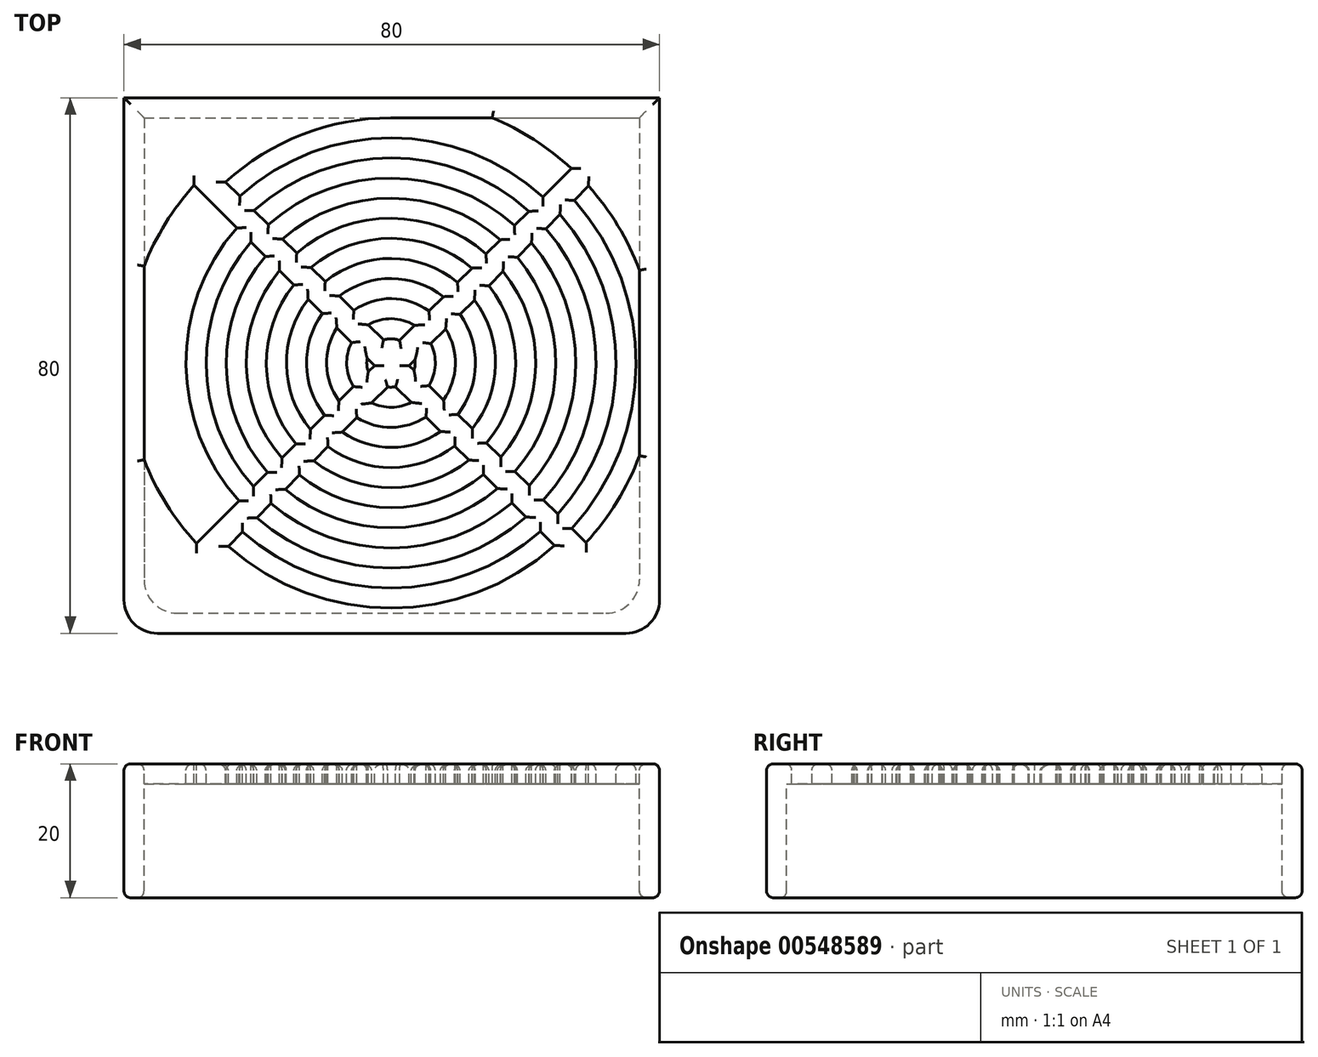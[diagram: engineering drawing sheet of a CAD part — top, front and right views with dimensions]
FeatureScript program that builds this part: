
annotation { "Feature Type Name" : "Feature", "Feature Type Description" : "" }
export const myFeature = defineFeature(function(context is Context, id is Id, definition is map)
    precondition{}
    {
        {
            var Q0;
            Q0=qCreatedBy(makeId("Front.planeOp"),FACE);
            var sketch = newSketch(context, id + "F0", { "sketchPlane" : qUnion([Q0])});
            skLineSegment(sketch, "E0.bottom", {"start": v(0, 0) * mm, "end": v(80, 0) * mm});
            skLineSegment(sketch, "E0.top", {"start": v(0, 20) * mm, "end": v(80, 20) * mm});
            skLineSegment(sketch, "E0.left", {"start": v(0, 0) * mm, "end": v(0, 20) * mm});
            skLineSegment(sketch, "E0.right", {"start": v(80, 0) * mm, "end": v(80, 20) * mm});
            skSolve(sketch);
        }
        {
            var Q0;
            Q0 = qSketchRegion(id + "F0", true);
            extrude(context, id + "F1", {"entities" : qUnion([Q0]), "depth" : 3 * mm, "offsetDistance" : 25 * mm});
        }
        {
            var Q0;
            Q0=makeQuery(id+"F1.opExtrude","SWEPT_FACE",FACE,{"disambiguationData":[OSD([sQuery(id+"F0.wireOp",EDGE,"E0.top")])]});
            var sketch = newSketch(context, id + "F2", { "sketchPlane" : qUnion([Q0])});
            skLineSegment(sketch, "E1.bottom", {"start": v(0, 0) * mm, "end": v(80, 0) * mm});
            skLineSegment(sketch, "E1.top", {"start": v(0, -80) * mm, "end": v(80, -80) * mm});
            skLineSegment(sketch, "E1.left", {"start": v(0, 0) * mm, "end": v(0, -80) * mm});
            skLineSegment(sketch, "E1.right", {"start": v(80, 0) * mm, "end": v(80, -80) * mm});
            skLineSegment(sketch, "E2.bottom", {"start": v(3, -3) * mm, "end": v(77, -3) * mm});
            skLineSegment(sketch, "E2.top", {"start": v(3, -77) * mm, "end": v(77, -77) * mm});
            skLineSegment(sketch, "E2.left", {"start": v(3, -3) * mm, "end": v(3, -77) * mm});
            skLineSegment(sketch, "E2.right", {"start": v(77, -3) * mm, "end": v(77, -77) * mm});
            skSolve(sketch);
        }
        {
            var Q0;
            Q0 = qSketchRegion(id + "F2", true);
            extrude(context, id + "F3", {"entities" : qUnion([Q0]), "operationType" : NewBodyOperationType.ADD, "oppositeDirection" : true, "depth" : 20 * mm, "offsetDistance" : 25 * mm});
        }
        {
            var Q0;
            Q0=makeQuery(id+"F3.opExtrude","SWEPT_EDGE",EDGE,{"disambiguationData":[OSD([sQuery(id+"F2.wireOp",EDGE,"E1.top"),sQuery(id+"F2.wireOp",EDGE,"E1.left")])]});
            var Q1;
            Q1=makeQuery(id+"F3.opExtrude","SWEPT_EDGE",EDGE,{"disambiguationData":[OSD([sQuery(id+"F2.wireOp",EDGE,"E1.top"),sQuery(id+"F2.wireOp",EDGE,"E1.right")])]});
            var Q2;
            Q2=makeQuery(id+"F3.opExtrude","SWEPT_EDGE",EDGE,{"disambiguationData":[OSD([sQuery(id+"F0.wireOp",EDGE,"E0.top"),sQuery(id+"F2.wireOp",EDGE,"E2.bottom"),sQuery(id+"F2.wireOp",EDGE,"E2.left")])]});
            var Q3;
            Q3=makeQuery(id+"F3.opExtrude","SWEPT_EDGE",EDGE,{"disambiguationData":[OSD([sQuery(id+"F2.wireOp",EDGE,"E2.top"),sQuery(id+"F2.wireOp",EDGE,"E2.left")])]});
            var Q4;
            Q4=makeQuery(id+"F3.opExtrude","SWEPT_EDGE",EDGE,{"disambiguationData":[OSD([sQuery(id+"F0.wireOp",EDGE,"E0.top"),sQuery(id+"F2.wireOp",EDGE,"E2.bottom"),sQuery(id+"F2.wireOp",EDGE,"E2.right")])]});
            var Q5;
            Q5=makeQuery(id+"F3.opExtrude","SWEPT_EDGE",EDGE,{"disambiguationData":[OSD([sQuery(id+"F2.wireOp",EDGE,"E2.top"),sQuery(id+"F2.wireOp",EDGE,"E2.right")])]});
            fillet(context, id + "F4", {"entities" : qUnion([Q0, Q1, Q2, Q3, Q4, Q5]), "radius" : 5 * mm, "tangentPropagation" : true, "allowEdgeOverflow" : false});
        }
        {
            var Q0;
            Q0=makeQuery(id+"F3.boolean.opBoolean","MERGE",FACE,{"derivedFrom":[makeQuery(id+"F1.opExtrude","SWEPT_FACE",FACE,{"disambiguationData":[OSD([sQuery(id+"F0.wireOp",EDGE,"E0.top")])]}),makeQuery(id+"F3.opExtrude","CAP_FACE",FACE,{"disambiguationData":[OSD([sQuery(id+"F2.wireOp",EDGE,"E1.bottom"),sQuery(id+"F2.wireOp",EDGE,"E1.top"),sQuery(id+"F2.wireOp",EDGE,"E1.left"),sQuery(id+"F2.wireOp",EDGE,"E1.right"),sQuery(id+"F2.wireOp",EDGE,"E2.bottom"),sQuery(id+"F2.wireOp",EDGE,"E2.top"),sQuery(id+"F2.wireOp",EDGE,"E2.left"),sQuery(id+"F2.wireOp",EDGE,"E2.right")])],"isStart":true})]});
            var sketch = newSketch(context, id + "F5", { "sketchPlane" : qUnion([Q0])});
            skLineSegment(sketch, "E3", {"start": v(4.46, -4.46) * mm, "end": v(75.54, -75) * mm});
            skPoint(sketch, "E3.endSnap0", {"position": v(75.54, -75.54) * mm});
            skLineSegment(sketch, "E4", {"start": v(75.54, -4.46) * mm, "end": v(4, -75) * mm});
            skPoint(sketch, "E5", {"position": v(39.88, -39.62) * mm});
            skCircle(sketch, "E6", {"center": v(39.88, -39.62) * mm, "radius": 39.62 * mm});
            skCircle(sketch, "E7", {"center": v(39.88, -39.62) * mm, "radius": 36.62 * mm});
            skCircle(sketch, "E8", {"center": v(39.88, -39.62) * mm, "radius": 33.62 * mm});
            skCircle(sketch, "E9", {"center": v(39.88, -39.62) * mm, "radius": 30.62 * mm});
            skCircle(sketch, "E10", {"center": v(39.88, -39.62) * mm, "radius": 27.62 * mm});
            skCircle(sketch, "E11", {"center": v(39.88, -39.62) * mm, "radius": 24.62 * mm});
            skCircle(sketch, "E12", {"center": v(39.88, -39.62) * mm, "radius": 21.62 * mm});
            skCircle(sketch, "E13", {"center": v(39.88, -39.62) * mm, "radius": 18.62 * mm});
            skCircle(sketch, "E14", {"center": v(39.88, -39.62) * mm, "radius": 15.62 * mm});
            skCircle(sketch, "E15", {"center": v(39.88, -39.62) * mm, "radius": 12.62 * mm});
            skCircle(sketch, "E16", {"center": v(39.88, -39.62) * mm, "radius": 9.62 * mm});
            skCircle(sketch, "E17", {"center": v(39.88, -39.62) * mm, "radius": 6.62 * mm});
            skCircle(sketch, "E18", {"center": v(39.88, -39.62) * mm, "radius": 3.62 * mm});
            skSolve(sketch);
        }
        {
            var Q0;
            {var subQ0=sQuery(id+"F5.wireOp",EDGE,"E6");var subQ1=sQuery(id+"F5.wireOp",EDGE,"E3");var subQ2=makeQuery(id+"F5.imprint","INTERSECT",VERTEX,{"disambiguationData":[OD(1.0)],"derivedFrom":[subQ1,subQ0]});Q0=makeQuery(id+"F5.imprint","IMPRINT",FACE,{"disambiguationData":[TD([[makeQuery(id+"F5.imprint","IMPRINT",EDGE,{"disambiguationData":[TD([[subQ2,-1.0]])],"derivedFrom":subQ1}),1.0]])]});}
            var Q1;
            {var subQ0=sQuery(id+"F5.wireOp",EDGE,"E6");var subQ1=sQuery(id+"F5.wireOp",EDGE,"E4");var subQ2=makeQuery(id+"F5.imprint","INTERSECT",VERTEX,{"disambiguationData":[OD(0.0)],"derivedFrom":[subQ1,subQ0]});Q1=makeQuery(id+"F5.imprint","IMPRINT",FACE,{"disambiguationData":[TD([[makeQuery(id+"F5.imprint","IMPRINT",EDGE,{"disambiguationData":[TD([[subQ2,-1.0]])],"derivedFrom":subQ1}),-1.0]])]});}
            var Q2;
            {var subQ0=sQuery(id+"F5.wireOp",EDGE,"E6");var subQ1=sQuery(id+"F5.wireOp",EDGE,"E3");var subQ2=makeQuery(id+"F5.imprint","INTERSECT",VERTEX,{"disambiguationData":[OD(0.0)],"derivedFrom":[subQ1,subQ0]});Q2=makeQuery(id+"F5.imprint","IMPRINT",FACE,{"disambiguationData":[TD([[makeQuery(id+"F5.imprint","IMPRINT",EDGE,{"disambiguationData":[TD([[subQ2,1.0]])],"derivedFrom":subQ1}),-1.0]])]});}
            var Q3;
            {var subQ0=sQuery(id+"F5.wireOp",EDGE,"E8");var subQ1=sQuery(id+"F5.wireOp",EDGE,"E3");var subQ2=makeQuery(id+"F5.imprint","INTERSECT",VERTEX,{"disambiguationData":[OD(0.0)],"derivedFrom":[subQ1,subQ0]});Q3=makeQuery(id+"F5.imprint","IMPRINT",FACE,{"disambiguationData":[TD([[makeQuery(id+"F5.imprint","IMPRINT",EDGE,{"disambiguationData":[TD([[subQ2,-1.0]])],"derivedFrom":subQ1}),1.0]])]});}
            var Q4;
            {var subQ0=sQuery(id+"F5.wireOp",EDGE,"E10");var subQ1=sQuery(id+"F5.wireOp",EDGE,"E3");var subQ2=makeQuery(id+"F5.imprint","INTERSECT",VERTEX,{"disambiguationData":[OD(0.0)],"derivedFrom":[subQ1,subQ0]});Q4=makeQuery(id+"F5.imprint","IMPRINT",FACE,{"disambiguationData":[TD([[makeQuery(id+"F5.imprint","IMPRINT",EDGE,{"disambiguationData":[TD([[subQ2,-1.0]])],"derivedFrom":subQ1}),1.0]])]});}
            var Q5;
            {var subQ0=sQuery(id+"F5.wireOp",EDGE,"E12");var subQ1=sQuery(id+"F5.wireOp",EDGE,"E3");var subQ2=makeQuery(id+"F5.imprint","INTERSECT",VERTEX,{"disambiguationData":[OD(0.0)],"derivedFrom":[subQ1,subQ0]});Q5=makeQuery(id+"F5.imprint","IMPRINT",FACE,{"disambiguationData":[TD([[makeQuery(id+"F5.imprint","IMPRINT",EDGE,{"disambiguationData":[TD([[subQ2,-1.0]])],"derivedFrom":subQ1}),1.0]])]});}
            var Q6;
            {var subQ0=sQuery(id+"F5.wireOp",EDGE,"E14");var subQ1=sQuery(id+"F5.wireOp",EDGE,"E3");var subQ2=makeQuery(id+"F5.imprint","INTERSECT",VERTEX,{"disambiguationData":[OD(0.0)],"derivedFrom":[subQ1,subQ0]});Q6=makeQuery(id+"F5.imprint","IMPRINT",FACE,{"disambiguationData":[TD([[makeQuery(id+"F5.imprint","IMPRINT",EDGE,{"disambiguationData":[TD([[subQ2,-1.0]])],"derivedFrom":subQ1}),1.0]])]});}
            var Q7;
            {var subQ0=sQuery(id+"F5.wireOp",EDGE,"E16");var subQ1=sQuery(id+"F5.wireOp",EDGE,"E3");var subQ2=makeQuery(id+"F5.imprint","INTERSECT",VERTEX,{"disambiguationData":[OD(0.0)],"derivedFrom":[subQ1,subQ0]});Q7=makeQuery(id+"F5.imprint","IMPRINT",FACE,{"disambiguationData":[TD([[makeQuery(id+"F5.imprint","IMPRINT",EDGE,{"disambiguationData":[TD([[subQ2,-1.0]])],"derivedFrom":subQ1}),1.0]])]});}
            var Q8;
            {var subQ0=sQuery(id+"F5.wireOp",EDGE,"E18");var subQ1=sQuery(id+"F5.wireOp",EDGE,"E3");var subQ2=makeQuery(id+"F5.imprint","INTERSECT",VERTEX,{"disambiguationData":[OD(0.0)],"derivedFrom":[subQ1,subQ0]});Q8=makeQuery(id+"F5.imprint","IMPRINT",FACE,{"disambiguationData":[TD([[makeQuery(id+"F5.imprint","IMPRINT",EDGE,{"disambiguationData":[TD([[subQ2,-1.0]])],"derivedFrom":subQ1}),1.0]])]});}
            var Q9;
            {var subQ0=sQuery(id+"F5.wireOp",EDGE,"E4");var subQ1=sQuery(id+"F5.wireOp",EDGE,"E3");var subQ2=makeQuery(id+"F5.imprint","INTERSECT",VERTEX,{"derivedFrom":[subQ1,subQ0]});Q9=makeQuery(id+"F5.imprint","IMPRINT",FACE,{"disambiguationData":[TD([[makeQuery(id+"F5.imprint","IMPRINT",EDGE,{"disambiguationData":[TD([[subQ2,-1.0]])],"derivedFrom":subQ1}),-1.0]])]});}
            var Q10;
            {var subQ0=sQuery(id+"F5.wireOp",EDGE,"E11");var subQ1=sQuery(id+"F5.wireOp",EDGE,"E3");var subQ2=makeQuery(id+"F5.imprint","INTERSECT",VERTEX,{"disambiguationData":[OD(1.0)],"derivedFrom":[subQ1,subQ0]});Q10=makeQuery(id+"F5.imprint","IMPRINT",FACE,{"disambiguationData":[TD([[makeQuery(id+"F5.imprint","IMPRINT",EDGE,{"disambiguationData":[TD([[subQ2,-1.0]])],"derivedFrom":subQ1}),-1.0]])]});}
            var Q11;
            {var subQ0=sQuery(id+"F5.wireOp",EDGE,"E9");var subQ1=sQuery(id+"F5.wireOp",EDGE,"E3");var subQ2=makeQuery(id+"F5.imprint","INTERSECT",VERTEX,{"disambiguationData":[OD(1.0)],"derivedFrom":[subQ1,subQ0]});Q11=makeQuery(id+"F5.imprint","IMPRINT",FACE,{"disambiguationData":[TD([[makeQuery(id+"F5.imprint","IMPRINT",EDGE,{"disambiguationData":[TD([[subQ2,-1.0]])],"derivedFrom":subQ1}),-1.0]])]});}
            var Q12;
            {var subQ0=sQuery(id+"F5.wireOp",EDGE,"E13");var subQ1=sQuery(id+"F5.wireOp",EDGE,"E3");var subQ2=makeQuery(id+"F5.imprint","INTERSECT",VERTEX,{"disambiguationData":[OD(1.0)],"derivedFrom":[subQ1,subQ0]});Q12=makeQuery(id+"F5.imprint","IMPRINT",FACE,{"disambiguationData":[TD([[makeQuery(id+"F5.imprint","IMPRINT",EDGE,{"disambiguationData":[TD([[subQ2,-1.0]])],"derivedFrom":subQ1}),-1.0]])]});}
            var Q13;
            {var subQ0=sQuery(id+"F5.wireOp",EDGE,"E15");var subQ1=sQuery(id+"F5.wireOp",EDGE,"E3");var subQ2=makeQuery(id+"F5.imprint","INTERSECT",VERTEX,{"disambiguationData":[OD(1.0)],"derivedFrom":[subQ1,subQ0]});Q13=makeQuery(id+"F5.imprint","IMPRINT",FACE,{"disambiguationData":[TD([[makeQuery(id+"F5.imprint","IMPRINT",EDGE,{"disambiguationData":[TD([[subQ2,-1.0]])],"derivedFrom":subQ1}),-1.0]])]});}
            var Q14;
            {var subQ0=sQuery(id+"F5.wireOp",EDGE,"E17");var subQ1=sQuery(id+"F5.wireOp",EDGE,"E3");var subQ2=makeQuery(id+"F5.imprint","INTERSECT",VERTEX,{"disambiguationData":[OD(1.0)],"derivedFrom":[subQ1,subQ0]});Q14=makeQuery(id+"F5.imprint","IMPRINT",FACE,{"disambiguationData":[TD([[makeQuery(id+"F5.imprint","IMPRINT",EDGE,{"disambiguationData":[TD([[subQ2,-1.0]])],"derivedFrom":subQ1}),-1.0]])]});}
            var Q15;
            {var subQ0=sQuery(id+"F5.wireOp",EDGE,"E18");var subQ1=sQuery(id+"F5.wireOp",EDGE,"E3");var subQ2=makeQuery(id+"F5.imprint","INTERSECT",VERTEX,{"disambiguationData":[OD(1.0)],"derivedFrom":[subQ1,subQ0]});Q15=makeQuery(id+"F5.imprint","IMPRINT",FACE,{"disambiguationData":[TD([[makeQuery(id+"F5.imprint","IMPRINT",EDGE,{"disambiguationData":[TD([[subQ2,-1.0]])],"derivedFrom":subQ1}),1.0]])]});}
            var Q16;
            {var subQ0=sQuery(id+"F5.wireOp",EDGE,"E16");var subQ1=sQuery(id+"F5.wireOp",EDGE,"E3");var subQ2=makeQuery(id+"F5.imprint","INTERSECT",VERTEX,{"disambiguationData":[OD(1.0)],"derivedFrom":[subQ1,subQ0]});Q16=makeQuery(id+"F5.imprint","IMPRINT",FACE,{"disambiguationData":[TD([[makeQuery(id+"F5.imprint","IMPRINT",EDGE,{"disambiguationData":[TD([[subQ2,-1.0]])],"derivedFrom":subQ1}),1.0]])]});}
            var Q17;
            {var subQ0=sQuery(id+"F5.wireOp",EDGE,"E14");var subQ1=sQuery(id+"F5.wireOp",EDGE,"E3");var subQ2=makeQuery(id+"F5.imprint","INTERSECT",VERTEX,{"disambiguationData":[OD(1.0)],"derivedFrom":[subQ1,subQ0]});Q17=makeQuery(id+"F5.imprint","IMPRINT",FACE,{"disambiguationData":[TD([[makeQuery(id+"F5.imprint","IMPRINT",EDGE,{"disambiguationData":[TD([[subQ2,-1.0]])],"derivedFrom":subQ1}),1.0]])]});}
            var Q18;
            {var subQ0=sQuery(id+"F5.wireOp",EDGE,"E12");var subQ1=sQuery(id+"F5.wireOp",EDGE,"E3");var subQ2=makeQuery(id+"F5.imprint","INTERSECT",VERTEX,{"disambiguationData":[OD(1.0)],"derivedFrom":[subQ1,subQ0]});Q18=makeQuery(id+"F5.imprint","IMPRINT",FACE,{"disambiguationData":[TD([[makeQuery(id+"F5.imprint","IMPRINT",EDGE,{"disambiguationData":[TD([[subQ2,-1.0]])],"derivedFrom":subQ1}),1.0]])]});}
            var Q19;
            {var subQ0=sQuery(id+"F5.wireOp",EDGE,"E10");var subQ1=sQuery(id+"F5.wireOp",EDGE,"E3");var subQ2=makeQuery(id+"F5.imprint","INTERSECT",VERTEX,{"disambiguationData":[OD(1.0)],"derivedFrom":[subQ1,subQ0]});Q19=makeQuery(id+"F5.imprint","IMPRINT",FACE,{"disambiguationData":[TD([[makeQuery(id+"F5.imprint","IMPRINT",EDGE,{"disambiguationData":[TD([[subQ2,-1.0]])],"derivedFrom":subQ1}),1.0]])]});}
            var Q20;
            {var subQ0=sQuery(id+"F5.wireOp",EDGE,"E8");var subQ1=sQuery(id+"F5.wireOp",EDGE,"E3");var subQ2=makeQuery(id+"F5.imprint","INTERSECT",VERTEX,{"disambiguationData":[OD(1.0)],"derivedFrom":[subQ1,subQ0]});Q20=makeQuery(id+"F5.imprint","IMPRINT",FACE,{"disambiguationData":[TD([[makeQuery(id+"F5.imprint","IMPRINT",EDGE,{"disambiguationData":[TD([[subQ2,-1.0]])],"derivedFrom":subQ1}),1.0]])]});}
            var Q21;
            {var subQ0=sQuery(id+"F5.wireOp",EDGE,"E4");var subQ6=sQuery(id+"F5.wireOp",EDGE,"E6");var subQ7=makeQuery(id+"F5.imprint","INTERSECT",VERTEX,{"disambiguationData":[OD(0.0)],"derivedFrom":[subQ0,subQ6]});Q21=makeQuery(id+"F5.imprint","IMPRINT",FACE,{"disambiguationData":[TD([[makeQuery(id+"F5.imprint","IMPRINT",EDGE,{"disambiguationData":[TD([[subQ7,1.0]])],"derivedFrom":subQ6}),-1.0]])]});}
            var Q22;
            {var subQ4=sQuery(id+"F5.wireOp",EDGE,"E6");var subQ6=makeQuery(id+"F5.imprint","INTERSECT",VERTEX,{"disambiguationData":[OD(0.0)],"derivedFrom":[sQuery(id+"F5.wireOp",EDGE,"E3"),subQ4]});Q22=makeQuery(id+"F5.imprint","IMPRINT",FACE,{"disambiguationData":[TD([[makeQuery(id+"F5.imprint","IMPRINT",EDGE,{"disambiguationData":[TD([[subQ6,1.0]])],"derivedFrom":subQ4}),-1.0]])]});}
            var Q23;
            {var subQ0=sQuery(id+"F5.wireOp",EDGE,"E4");var subQ6=sQuery(id+"F5.wireOp",EDGE,"E6");var subQ7=makeQuery(id+"F5.imprint","INTERSECT",VERTEX,{"disambiguationData":[OD(0.0)],"derivedFrom":[subQ0,subQ6]});Q23=makeQuery(id+"F5.imprint","IMPRINT",FACE,{"disambiguationData":[TD([[makeQuery(id+"F5.imprint","IMPRINT",EDGE,{"disambiguationData":[TD([[subQ7,-1.0]])],"derivedFrom":subQ6}),-1.0]])]});}
            var Q24;
            {var subQ0=sQuery(id+"F5.wireOp",EDGE,"E17");var subQ1=sQuery(id+"F5.wireOp",EDGE,"E3");var subQ2=makeQuery(id+"F5.imprint","INTERSECT",VERTEX,{"disambiguationData":[OD(0.0)],"derivedFrom":[subQ1,subQ0]});Q24=makeQuery(id+"F5.imprint","IMPRINT",FACE,{"disambiguationData":[TD([[makeQuery(id+"F5.imprint","IMPRINT",EDGE,{"disambiguationData":[TD([[subQ2,-1.0]])],"derivedFrom":subQ1}),-1.0]])]});}
            var Q25;
            {var subQ0=sQuery(id+"F5.wireOp",EDGE,"E15");var subQ1=sQuery(id+"F5.wireOp",EDGE,"E3");var subQ2=makeQuery(id+"F5.imprint","INTERSECT",VERTEX,{"disambiguationData":[OD(0.0)],"derivedFrom":[subQ1,subQ0]});Q25=makeQuery(id+"F5.imprint","IMPRINT",FACE,{"disambiguationData":[TD([[makeQuery(id+"F5.imprint","IMPRINT",EDGE,{"disambiguationData":[TD([[subQ2,-1.0]])],"derivedFrom":subQ1}),-1.0]])]});}
            var Q26;
            {var subQ0=sQuery(id+"F5.wireOp",EDGE,"E13");var subQ1=sQuery(id+"F5.wireOp",EDGE,"E3");var subQ2=makeQuery(id+"F5.imprint","INTERSECT",VERTEX,{"disambiguationData":[OD(0.0)],"derivedFrom":[subQ1,subQ0]});Q26=makeQuery(id+"F5.imprint","IMPRINT",FACE,{"disambiguationData":[TD([[makeQuery(id+"F5.imprint","IMPRINT",EDGE,{"disambiguationData":[TD([[subQ2,-1.0]])],"derivedFrom":subQ1}),-1.0]])]});}
            var Q27;
            {var subQ0=sQuery(id+"F5.wireOp",EDGE,"E11");var subQ1=sQuery(id+"F5.wireOp",EDGE,"E3");var subQ2=makeQuery(id+"F5.imprint","INTERSECT",VERTEX,{"disambiguationData":[OD(0.0)],"derivedFrom":[subQ1,subQ0]});Q27=makeQuery(id+"F5.imprint","IMPRINT",FACE,{"disambiguationData":[TD([[makeQuery(id+"F5.imprint","IMPRINT",EDGE,{"disambiguationData":[TD([[subQ2,-1.0]])],"derivedFrom":subQ1}),-1.0]])]});}
            var Q28;
            {var subQ0=sQuery(id+"F5.wireOp",EDGE,"E9");var subQ1=sQuery(id+"F5.wireOp",EDGE,"E3");var subQ2=makeQuery(id+"F5.imprint","INTERSECT",VERTEX,{"disambiguationData":[OD(0.0)],"derivedFrom":[subQ1,subQ0]});Q28=makeQuery(id+"F5.imprint","IMPRINT",FACE,{"disambiguationData":[TD([[makeQuery(id+"F5.imprint","IMPRINT",EDGE,{"disambiguationData":[TD([[subQ2,-1.0]])],"derivedFrom":subQ1}),-1.0]])]});}
            var Q29;
            {var subQ0=sQuery(id+"F5.wireOp",EDGE,"E4");var subQ5=sQuery(id+"F5.wireOp",EDGE,"E6");var subQ6=makeQuery(id+"F5.imprint","INTERSECT",VERTEX,{"disambiguationData":[OD(1.0)],"derivedFrom":[subQ0,subQ5]});Q29=makeQuery(id+"F5.imprint","IMPRINT",FACE,{"disambiguationData":[TD([[makeQuery(id+"F5.imprint","IMPRINT",EDGE,{"disambiguationData":[TD([[subQ6,1.0]])],"derivedFrom":subQ5}),-1.0]])]});}
            var Q30;
            {var subQ0=sQuery(id+"F5.wireOp",EDGE,"E3");var subQ6=sQuery(id+"F5.wireOp",EDGE,"E6");var subQ7=makeQuery(id+"F5.imprint","INTERSECT",VERTEX,{"disambiguationData":[OD(1.0)],"derivedFrom":[subQ0,subQ6]});Q30=makeQuery(id+"F5.imprint","IMPRINT",FACE,{"disambiguationData":[TD([[makeQuery(id+"F5.imprint","IMPRINT",EDGE,{"disambiguationData":[TD([[subQ7,-1.0]])],"derivedFrom":subQ6}),-1.0]])]});}
            var Q31;
            {var subQ0=sQuery(id+"F5.wireOp",EDGE,"E4");var subQ5=sQuery(id+"F5.wireOp",EDGE,"E6");var subQ6=makeQuery(id+"F5.imprint","INTERSECT",VERTEX,{"disambiguationData":[OD(1.0)],"derivedFrom":[subQ0,subQ5]});Q31=makeQuery(id+"F5.imprint","IMPRINT",FACE,{"disambiguationData":[TD([[makeQuery(id+"F5.imprint","IMPRINT",EDGE,{"disambiguationData":[TD([[subQ6,-1.0]])],"derivedFrom":subQ5}),-1.0]])]});}
            var Q32;
            {var subQ0=sQuery(id+"F5.wireOp",EDGE,"E3");var subQ6=sQuery(id+"F5.wireOp",EDGE,"E6");var subQ7=makeQuery(id+"F5.imprint","INTERSECT",VERTEX,{"disambiguationData":[OD(1.0)],"derivedFrom":[subQ0,subQ6]});Q32=makeQuery(id+"F5.imprint","IMPRINT",FACE,{"disambiguationData":[TD([[makeQuery(id+"F5.imprint","IMPRINT",EDGE,{"disambiguationData":[TD([[subQ7,1.0]])],"derivedFrom":subQ6}),-1.0]])]});}
            var Q33;
            {var subQ0=sQuery(id+"F5.wireOp",EDGE,"E7");var subQ1=sQuery(id+"F5.wireOp",EDGE,"E3");var subQ2=makeQuery(id+"F5.imprint","INTERSECT",VERTEX,{"disambiguationData":[OD(0.0)],"derivedFrom":[subQ1,subQ0]});Q33=makeQuery(id+"F5.imprint","IMPRINT",FACE,{"disambiguationData":[TD([[makeQuery(id+"F5.imprint","IMPRINT",EDGE,{"disambiguationData":[TD([[subQ2,-1.0]])],"derivedFrom":subQ1}),-1.0]])]});}
            extrude(context, id + "F6", {"entities" : qUnion([Q0, Q1, Q2, Q3, Q4, Q5, Q6, Q7, Q8, Q9, Q10, Q11, Q12, Q13, Q14, Q15, Q16, Q17, Q18, Q19, Q20, Q21, Q22, Q23, Q24, Q25, Q26, Q27, Q28, Q29, Q30, Q31, Q32, Q33]), "operationType" : NewBodyOperationType.ADD, "oppositeDirection" : true, "depth" : 3 * mm, "offsetDistance" : 25 * mm});
        }
        {
            var Q0;
            {var subQ0=sQuery(id+"F5.wireOp",EDGE,"E7");var subQ1=sQuery(id+"F5.wireOp",EDGE,"E6");var subQ2=sQuery(id+"F5.wireOp",EDGE,"E4");var subQ3=sQuery(id+"F2.wireOp",EDGE,"E2.right");var subQ4=sQuery(id+"F2.wireOp",EDGE,"E2.left");var subQ5=sQuery(id+"F2.wireOp",EDGE,"E2.top");var subQ6=sQuery(id+"F2.wireOp",EDGE,"E2.bottom");var subQ7=sQuery(id+"F2.wireOp",EDGE,"E1.right");var subQ8=sQuery(id+"F2.wireOp",EDGE,"E1.left");var subQ9=sQuery(id+"F2.wireOp",EDGE,"E1.top");var subQ10=sQuery(id+"F2.wireOp",EDGE,"E1.bottom");var subQ11=sQuery(id+"F0.wireOp",EDGE,"E0.top");var subQ12=sQuery(id+"F5.wireOp",EDGE,"E3");Q0=makeQuery(id+"F6.boolean.opBoolean","MERGE",FACE,{"derivedFrom":[makeQuery(id+"F3.boolean.opBoolean","MERGE",FACE,{"derivedFrom":[makeQuery(id+"F1.opExtrude","SWEPT_FACE",FACE,{"disambiguationData":[OSD([subQ11])]}),makeQuery(id+"F3.opExtrude","CAP_FACE",FACE,{"disambiguationData":[OSD([subQ10,subQ9,subQ8,subQ7,subQ6,subQ5,subQ4,subQ3])],"isStart":true})]}),makeQuery(id+"F6.opExtrude","CAP_FACE",FACE,{"disambiguationData":[OSD([subQ11,subQ10,subQ9,subQ8,subQ7,subQ6,subQ5,subQ4,subQ3,subQ12,subQ1,subQ0])],"isStart":true}),makeQuery(id+"F6.opExtrude","CAP_FACE",FACE,{"disambiguationData":[OSD([subQ11,subQ10,subQ9,subQ8,subQ7,subQ6,subQ5,subQ4,subQ3,subQ12,subQ2,subQ1,subQ0])],"isStart":true}),makeQuery(id+"F6.opExtrude","CAP_FACE",FACE,{"disambiguationData":[OSD([subQ11,subQ10,subQ9,subQ8,subQ7,subQ6,subQ5,subQ4,subQ3,subQ2,subQ1,subQ0])],"isStart":true})]});}
            var sketch = newSketch(context, id + "F7", { "sketchPlane" : qUnion([Q0])});
            skLineSegment(sketch, "E19", {"start": v(2.58, 0) * mm, "end": v(79.58, -77) * mm});
            skLineSegment(sketch, "E20", {"start": v(79.58, -77) * mm, "end": v(77, -79.58) * mm});
            skLineSegment(sketch, "E21", {"start": v(77, -79.58) * mm, "end": v(0, -2.58) * mm});
            skLineSegment(sketch, "E22", {"start": v(0, -2.58) * mm, "end": v(2.58, 0) * mm});
            skLineSegment(sketch, "E23", {"start": v(77.42, 0) * mm, "end": v(80, -2.58) * mm});
            skLineSegment(sketch, "E24", {"start": v(80, -2.58) * mm, "end": v(3, -79.58) * mm});
            skLineSegment(sketch, "E25", {"start": v(3, -79.58) * mm, "end": v(0.42, -77) * mm});
            skLineSegment(sketch, "E26", {"start": v(0.42, -77) * mm, "end": v(77.42, 0) * mm});
            skSolve(sketch);
        }
        {
            var Q0;
            Q0 = qSketchRegion(id + "F7", true);
            extrude(context, id + "F8", {"entities" : qUnion([Q0]), "operationType" : NewBodyOperationType.ADD, "oppositeDirection" : true, "depth" : 3 * mm, "offsetDistance" : 25 * mm});
        }
        {
            var Q0;
            Q0=makeQuery(id+"FZaE8QNVp6XG5ye_1.opExtrude","CAP_EDGE",EDGE,{"disambiguationData":[OSD([sQuery(id+"FQdyxd8xbATGqtn_1.wireOp",EDGE,"FlZFNKmO-1mFb-dZK1-pEXj-0cqHaFgLSyFe")])],"isStart":true});
            var Q1;
            Q1=makeQuery(id+"FZaE8QNVp6XG5ye_1.opExtrude","CAP_EDGE",EDGE,{"disambiguationData":[OSD([sQuery(id+"FQdyxd8xbATGqtn_1.wireOp",EDGE,"FlZFNKmO-1mFb-dZK1-pEXj-0cqHaFgLSyFe")])],"isStart":false});
            var Q2;
            {var subQ0=sQuery(id+"F5.wireOp",EDGE,"E7");var subQ1=sQuery(id+"F5.wireOp",EDGE,"E6");var subQ2=sQuery(id+"F5.wireOp",EDGE,"E4");var subQ3=sQuery(id+"F2.wireOp",EDGE,"E2.right");var subQ4=sQuery(id+"F2.wireOp",EDGE,"E2.left");var subQ5=sQuery(id+"F2.wireOp",EDGE,"E2.top");var subQ6=sQuery(id+"F2.wireOp",EDGE,"E2.bottom");var subQ7=sQuery(id+"F2.wireOp",EDGE,"E1.right");var subQ8=sQuery(id+"F2.wireOp",EDGE,"E1.left");var subQ9=sQuery(id+"F2.wireOp",EDGE,"E1.top");var subQ10=sQuery(id+"F2.wireOp",EDGE,"E1.bottom");var subQ11=sQuery(id+"F0.wireOp",EDGE,"E0.top");var subQ12=sQuery(id+"F5.wireOp",EDGE,"E3");var subQ13=sQuery(id+"F5.wireOp",EDGE,"E8");var subQ14=makeQuery(id+"F5.imprint","INTERSECT",VERTEX,{"disambiguationData":[OD(1.0)],"derivedFrom":[subQ12,subQ13]});var subQ15=makeQuery(id+"F5.imprint","INTERSECT",VERTEX,{"disambiguationData":[OD(0.0)],"derivedFrom":[subQ2,subQ13]});var subQ16=makeQuery(id+"F5.imprint","INTERSECT",VERTEX,{"disambiguationData":[OD(1.0)],"derivedFrom":[subQ12,subQ0]});var subQ17=makeQuery(id+"F5.imprint","INTERSECT",VERTEX,{"disambiguationData":[OD(0.0)],"derivedFrom":[subQ2,subQ0]});var subQ18=sQuery(id+"F5.wireOp",EDGE,"E9");var subQ19=makeQuery(id+"F5.imprint","INTERSECT",VERTEX,{"disambiguationData":[OD(1.0)],"derivedFrom":[subQ12,subQ18]});var subQ20=makeQuery(id+"F5.imprint","INTERSECT",VERTEX,{"disambiguationData":[OD(1.0)],"derivedFrom":[subQ2,subQ18]});var subQ21=makeQuery(id+"F5.imprint","INTERSECT",VERTEX,{"disambiguationData":[OD(1.0)],"derivedFrom":[subQ2,subQ13]});var subQ22=sQuery(id+"F5.wireOp",EDGE,"E10");var subQ23=makeQuery(id+"F5.imprint","INTERSECT",VERTEX,{"disambiguationData":[OD(1.0)],"derivedFrom":[subQ12,subQ22]});var subQ24=makeQuery(id+"F5.imprint","INTERSECT",VERTEX,{"disambiguationData":[OD(0.0)],"derivedFrom":[subQ2,subQ22]});var subQ25=makeQuery(id+"F5.imprint","INTERSECT",VERTEX,{"disambiguationData":[OD(0.0)],"derivedFrom":[subQ2,subQ18]});var subQ26=sQuery(id+"F5.wireOp",EDGE,"E11");var subQ27=makeQuery(id+"F5.imprint","INTERSECT",VERTEX,{"disambiguationData":[OD(1.0)],"derivedFrom":[subQ12,subQ26]});var subQ28=makeQuery(id+"F5.imprint","INTERSECT",VERTEX,{"disambiguationData":[OD(1.0)],"derivedFrom":[subQ2,subQ26]});var subQ29=makeQuery(id+"F5.imprint","INTERSECT",VERTEX,{"disambiguationData":[OD(1.0)],"derivedFrom":[subQ2,subQ22]});var subQ30=sQuery(id+"F5.wireOp",EDGE,"E12");var subQ31=makeQuery(id+"F5.imprint","INTERSECT",VERTEX,{"disambiguationData":[OD(1.0)],"derivedFrom":[subQ12,subQ30]});var subQ32=makeQuery(id+"F5.imprint","INTERSECT",VERTEX,{"disambiguationData":[OD(0.0)],"derivedFrom":[subQ2,subQ30]});var subQ33=makeQuery(id+"F5.imprint","INTERSECT",VERTEX,{"disambiguationData":[OD(0.0)],"derivedFrom":[subQ2,subQ26]});var subQ34=sQuery(id+"F5.wireOp",EDGE,"E13");var subQ35=makeQuery(id+"F5.imprint","INTERSECT",VERTEX,{"disambiguationData":[OD(1.0)],"derivedFrom":[subQ12,subQ34]});var subQ36=makeQuery(id+"F5.imprint","INTERSECT",VERTEX,{"disambiguationData":[OD(1.0)],"derivedFrom":[subQ2,subQ34]});var subQ37=makeQuery(id+"F5.imprint","INTERSECT",VERTEX,{"disambiguationData":[OD(1.0)],"derivedFrom":[subQ2,subQ30]});var subQ38=sQuery(id+"F5.wireOp",EDGE,"E14");var subQ39=makeQuery(id+"F5.imprint","INTERSECT",VERTEX,{"disambiguationData":[OD(1.0)],"derivedFrom":[subQ12,subQ38]});var subQ40=makeQuery(id+"F5.imprint","INTERSECT",VERTEX,{"disambiguationData":[OD(0.0)],"derivedFrom":[subQ2,subQ38]});var subQ41=makeQuery(id+"F5.imprint","INTERSECT",VERTEX,{"disambiguationData":[OD(0.0)],"derivedFrom":[subQ2,subQ34]});var subQ42=sQuery(id+"F5.wireOp",EDGE,"E15");var subQ43=makeQuery(id+"F5.imprint","INTERSECT",VERTEX,{"disambiguationData":[OD(1.0)],"derivedFrom":[subQ12,subQ42]});var subQ44=makeQuery(id+"F5.imprint","INTERSECT",VERTEX,{"disambiguationData":[OD(1.0)],"derivedFrom":[subQ2,subQ42]});var subQ45=makeQuery(id+"F5.imprint","INTERSECT",VERTEX,{"disambiguationData":[OD(1.0)],"derivedFrom":[subQ2,subQ38]});var subQ46=sQuery(id+"F5.wireOp",EDGE,"E16");var subQ47=makeQuery(id+"F5.imprint","INTERSECT",VERTEX,{"disambiguationData":[OD(1.0)],"derivedFrom":[subQ12,subQ46]});var subQ48=makeQuery(id+"F5.imprint","INTERSECT",VERTEX,{"disambiguationData":[OD(0.0)],"derivedFrom":[subQ2,subQ46]});var subQ49=makeQuery(id+"F5.imprint","INTERSECT",VERTEX,{"disambiguationData":[OD(0.0)],"derivedFrom":[subQ2,subQ42]});var subQ50=sQuery(id+"F5.wireOp",EDGE,"E17");var subQ51=makeQuery(id+"F5.imprint","INTERSECT",VERTEX,{"disambiguationData":[OD(1.0)],"derivedFrom":[subQ12,subQ50]});var subQ52=makeQuery(id+"F5.imprint","INTERSECT",VERTEX,{"disambiguationData":[OD(1.0)],"derivedFrom":[subQ2,subQ50]});var subQ53=makeQuery(id+"F5.imprint","INTERSECT",VERTEX,{"disambiguationData":[OD(1.0)],"derivedFrom":[subQ2,subQ46]});var subQ54=sQuery(id+"F5.wireOp",EDGE,"E18");var subQ55=makeQuery(id+"F5.imprint","INTERSECT",VERTEX,{"disambiguationData":[OD(1.0)],"derivedFrom":[subQ12,subQ54]});var subQ57=makeQuery(id+"F5.imprint","INTERSECT",VERTEX,{"disambiguationData":[OD(0.0)],"derivedFrom":[subQ2,subQ50]});var subQ58=makeQuery(id+"F5.imprint","INTERSECT",VERTEX,{"disambiguationData":[OD(1.0)],"derivedFrom":[subQ2,subQ54]});var subQ59=makeQuery(id+"F5.imprint","INTERSECT",VERTEX,{"derivedFrom":[subQ12,subQ2]});var subQ60=makeQuery(id+"F5.imprint","INTERSECT",VERTEX,{"disambiguationData":[OD(0.0)],"derivedFrom":[subQ12,subQ54]});var subQ61=makeQuery(id+"F5.imprint","INTERSECT",VERTEX,{"disambiguationData":[OD(0.0)],"derivedFrom":[subQ12,subQ50]});var subQ62=makeQuery(id+"F5.imprint","INTERSECT",VERTEX,{"disambiguationData":[OD(0.0)],"derivedFrom":[subQ12,subQ46]});var subQ63=makeQuery(id+"F5.imprint","INTERSECT",VERTEX,{"disambiguationData":[OD(0.0)],"derivedFrom":[subQ12,subQ42]});var subQ64=makeQuery(id+"F5.imprint","INTERSECT",VERTEX,{"disambiguationData":[OD(0.0)],"derivedFrom":[subQ12,subQ38]});var subQ65=makeQuery(id+"F5.imprint","INTERSECT",VERTEX,{"disambiguationData":[OD(0.0)],"derivedFrom":[subQ12,subQ34]});var subQ66=makeQuery(id+"F5.imprint","INTERSECT",VERTEX,{"disambiguationData":[OD(0.0)],"derivedFrom":[subQ12,subQ30]});var subQ67=makeQuery(id+"F5.imprint","INTERSECT",VERTEX,{"disambiguationData":[OD(0.0)],"derivedFrom":[subQ12,subQ26]});var subQ68=makeQuery(id+"F5.imprint","INTERSECT",VERTEX,{"disambiguationData":[OD(0.0)],"derivedFrom":[subQ12,subQ22]});var subQ69=makeQuery(id+"F5.imprint","INTERSECT",VERTEX,{"disambiguationData":[OD(0.0)],"derivedFrom":[subQ12,subQ18]});var subQ70=makeQuery(id+"F5.imprint","INTERSECT",VERTEX,{"disambiguationData":[OD(0.0)],"derivedFrom":[subQ12,subQ13]});var subQ71=makeQuery(id+"F5.imprint","INTERSECT",VERTEX,{"disambiguationData":[OD(0.0)],"derivedFrom":[subQ12,subQ0]});Q2=makeQuery(id+"FZaE8QNVp6XG5ye_1.boolean.opBoolean","MERGE",FACE,{"derivedFrom":[makeQuery(id+"F8.boolean.opBoolean","MERGE",FACE,{"derivedFrom":[makeQuery(id+"F6.opExtrude","CAP_FACE",FACE,{"disambiguationData":[OSD([subQ12,subQ2,subQ0,subQ13]),TDD([makeQuery(id+"F5.imprint","IMPRINT",EDGE,{"disambiguationData":[TD([[subQ71,-1.0]])],"derivedFrom":subQ12}),makeQuery(id+"F5.imprint","IMPRINT",EDGE,{"disambiguationData":[TD([[subQ21,-1.0]])],"derivedFrom":subQ2}),makeQuery(id+"F5.imprint","IMPRINT",EDGE,{"disambiguationData":[TD([[subQ71,-1.0]])],"derivedFrom":subQ0}),makeQuery(id+"F5.imprint","IMPRINT",EDGE,{"disambiguationData":[TD([[subQ70,-1.0]])],"derivedFrom":subQ13})])],"isStart":true}),makeQuery(id+"F6.opExtrude","CAP_FACE",FACE,{"disambiguationData":[OSD([subQ12,subQ2,subQ13,subQ18]),TDD([makeQuery(id+"F5.imprint","IMPRINT",EDGE,{"disambiguationData":[TD([[subQ70,-1.0]])],"derivedFrom":subQ12}),makeQuery(id+"F5.imprint","IMPRINT",EDGE,{"disambiguationData":[TD([[subQ15,-1.0]])],"derivedFrom":subQ2}),makeQuery(id+"F5.imprint","IMPRINT",EDGE,{"disambiguationData":[TD([[subQ70,1.0]])],"derivedFrom":subQ13}),makeQuery(id+"F5.imprint","IMPRINT",EDGE,{"disambiguationData":[TD([[subQ69,1.0]])],"derivedFrom":subQ18})])],"isStart":true}),makeQuery(id+"F6.opExtrude","CAP_FACE",FACE,{"disambiguationData":[OSD([subQ12,subQ2,subQ18,subQ22]),TDD([makeQuery(id+"F5.imprint","IMPRINT",EDGE,{"disambiguationData":[TD([[subQ69,-1.0]])],"derivedFrom":subQ12}),makeQuery(id+"F5.imprint","IMPRINT",EDGE,{"disambiguationData":[TD([[subQ29,-1.0]])],"derivedFrom":subQ2}),makeQuery(id+"F5.imprint","IMPRINT",EDGE,{"disambiguationData":[TD([[subQ69,-1.0]])],"derivedFrom":subQ18}),makeQuery(id+"F5.imprint","IMPRINT",EDGE,{"disambiguationData":[TD([[subQ68,-1.0]])],"derivedFrom":subQ22})])],"isStart":true}),makeQuery(id+"F6.opExtrude","CAP_FACE",FACE,{"disambiguationData":[OSD([subQ12,subQ2,subQ22,subQ26]),TDD([makeQuery(id+"F5.imprint","IMPRINT",EDGE,{"disambiguationData":[TD([[subQ68,-1.0]])],"derivedFrom":subQ12}),makeQuery(id+"F5.imprint","IMPRINT",EDGE,{"disambiguationData":[TD([[subQ24,-1.0]])],"derivedFrom":subQ2}),makeQuery(id+"F5.imprint","IMPRINT",EDGE,{"disambiguationData":[TD([[subQ68,1.0]])],"derivedFrom":subQ22}),makeQuery(id+"F5.imprint","IMPRINT",EDGE,{"disambiguationData":[TD([[subQ67,1.0]])],"derivedFrom":subQ26})])],"isStart":true}),makeQuery(id+"F6.opExtrude","CAP_FACE",FACE,{"disambiguationData":[OSD([subQ12,subQ2,subQ26,subQ30]),TDD([makeQuery(id+"F5.imprint","IMPRINT",EDGE,{"disambiguationData":[TD([[subQ67,-1.0]])],"derivedFrom":subQ12}),makeQuery(id+"F5.imprint","IMPRINT",EDGE,{"disambiguationData":[TD([[subQ37,-1.0]])],"derivedFrom":subQ2}),makeQuery(id+"F5.imprint","IMPRINT",EDGE,{"disambiguationData":[TD([[subQ67,-1.0]])],"derivedFrom":subQ26}),makeQuery(id+"F5.imprint","IMPRINT",EDGE,{"disambiguationData":[TD([[subQ66,-1.0]])],"derivedFrom":subQ30})])],"isStart":true}),makeQuery(id+"F6.opExtrude","CAP_FACE",FACE,{"disambiguationData":[OSD([subQ12,subQ2,subQ30,subQ34]),TDD([makeQuery(id+"F5.imprint","IMPRINT",EDGE,{"disambiguationData":[TD([[subQ66,-1.0]])],"derivedFrom":subQ12}),makeQuery(id+"F5.imprint","IMPRINT",EDGE,{"disambiguationData":[TD([[subQ32,-1.0]])],"derivedFrom":subQ2}),makeQuery(id+"F5.imprint","IMPRINT",EDGE,{"disambiguationData":[TD([[subQ66,1.0]])],"derivedFrom":subQ30}),makeQuery(id+"F5.imprint","IMPRINT",EDGE,{"disambiguationData":[TD([[subQ65,1.0]])],"derivedFrom":subQ34})])],"isStart":true}),makeQuery(id+"F6.opExtrude","CAP_FACE",FACE,{"disambiguationData":[OSD([subQ12,subQ2,subQ34,subQ38]),TDD([makeQuery(id+"F5.imprint","IMPRINT",EDGE,{"disambiguationData":[TD([[subQ65,-1.0]])],"derivedFrom":subQ12}),makeQuery(id+"F5.imprint","IMPRINT",EDGE,{"disambiguationData":[TD([[subQ45,-1.0]])],"derivedFrom":subQ2}),makeQuery(id+"F5.imprint","IMPRINT",EDGE,{"disambiguationData":[TD([[subQ65,-1.0]])],"derivedFrom":subQ34}),makeQuery(id+"F5.imprint","IMPRINT",EDGE,{"disambiguationData":[TD([[subQ64,-1.0]])],"derivedFrom":subQ38})])],"isStart":true}),makeQuery(id+"F6.opExtrude","CAP_FACE",FACE,{"disambiguationData":[OSD([subQ12,subQ2,subQ38,subQ42]),TDD([makeQuery(id+"F5.imprint","IMPRINT",EDGE,{"disambiguationData":[TD([[subQ64,-1.0]])],"derivedFrom":subQ12}),makeQuery(id+"F5.imprint","IMPRINT",EDGE,{"disambiguationData":[TD([[subQ40,-1.0]])],"derivedFrom":subQ2}),makeQuery(id+"F5.imprint","IMPRINT",EDGE,{"disambiguationData":[TD([[subQ64,1.0]])],"derivedFrom":subQ38}),makeQuery(id+"F5.imprint","IMPRINT",EDGE,{"disambiguationData":[TD([[subQ63,1.0]])],"derivedFrom":subQ42})])],"isStart":true}),makeQuery(id+"F6.opExtrude","CAP_FACE",FACE,{"disambiguationData":[OSD([subQ12,subQ2,subQ42,subQ46]),TDD([makeQuery(id+"F5.imprint","IMPRINT",EDGE,{"disambiguationData":[TD([[subQ63,-1.0]])],"derivedFrom":subQ12}),makeQuery(id+"F5.imprint","IMPRINT",EDGE,{"disambiguationData":[TD([[subQ53,-1.0]])],"derivedFrom":subQ2}),makeQuery(id+"F5.imprint","IMPRINT",EDGE,{"disambiguationData":[TD([[subQ63,-1.0]])],"derivedFrom":subQ42}),makeQuery(id+"F5.imprint","IMPRINT",EDGE,{"disambiguationData":[TD([[subQ62,-1.0]])],"derivedFrom":subQ46})])],"isStart":true}),makeQuery(id+"F6.opExtrude","CAP_FACE",FACE,{"disambiguationData":[OSD([subQ12,subQ2,subQ46,subQ50]),TDD([makeQuery(id+"F5.imprint","IMPRINT",EDGE,{"disambiguationData":[TD([[subQ62,-1.0]])],"derivedFrom":subQ12}),makeQuery(id+"F5.imprint","IMPRINT",EDGE,{"disambiguationData":[TD([[subQ48,-1.0]])],"derivedFrom":subQ2}),makeQuery(id+"F5.imprint","IMPRINT",EDGE,{"disambiguationData":[TD([[subQ62,1.0]])],"derivedFrom":subQ46}),makeQuery(id+"F5.imprint","IMPRINT",EDGE,{"disambiguationData":[TD([[subQ61,1.0]])],"derivedFrom":subQ50})])],"isStart":true}),makeQuery(id+"F6.opExtrude","CAP_FACE",FACE,{"disambiguationData":[OSD([subQ12,subQ2,subQ50,subQ54]),TDD([makeQuery(id+"F5.imprint","IMPRINT",EDGE,{"disambiguationData":[TD([[subQ61,-1.0]])],"derivedFrom":subQ12}),makeQuery(id+"F5.imprint","IMPRINT",EDGE,{"disambiguationData":[TD([[subQ58,-1.0]])],"derivedFrom":subQ2}),makeQuery(id+"F5.imprint","IMPRINT",EDGE,{"disambiguationData":[TD([[subQ61,-1.0]])],"derivedFrom":subQ50}),makeQuery(id+"F5.imprint","IMPRINT",EDGE,{"disambiguationData":[TD([[subQ60,-1.0]])],"derivedFrom":subQ54})])],"isStart":true}),makeQuery(id+"F6.opExtrude","CAP_FACE",FACE,{"disambiguationData":[OSD([subQ12,subQ2,subQ54]),TDD([makeQuery(id+"F5.imprint","IMPRINT",EDGE,{"disambiguationData":[TD([[subQ60,-1.0]])],"derivedFrom":subQ12}),makeQuery(id+"F5.imprint","IMPRINT",EDGE,{"disambiguationData":[TD([[subQ59,1.0]])],"derivedFrom":subQ2}),makeQuery(id+"F5.imprint","IMPRINT",EDGE,{"disambiguationData":[TD([[subQ60,1.0]])],"derivedFrom":subQ54})])],"isStart":true}),makeQuery(id+"F6.opExtrude","CAP_FACE",FACE,{"disambiguationData":[OSD([subQ12,subQ2,subQ54]),TDD([makeQuery(id+"F5.imprint","IMPRINT",EDGE,{"disambiguationData":[TD([[subQ59,-1.0]])],"derivedFrom":subQ12}),makeQuery(id+"F5.imprint","IMPRINT",EDGE,{"disambiguationData":[TD([[subQ59,-1.0]])],"derivedFrom":subQ2}),makeQuery(id+"F5.imprint","IMPRINT",EDGE,{"disambiguationData":[TD([[subQ55,1.0]])],"derivedFrom":subQ54})])],"isStart":true}),makeQuery(id+"F6.opExtrude","CAP_FACE",FACE,{"disambiguationData":[OSD([subQ12,subQ2,subQ50,subQ54]),TDD([makeQuery(id+"F5.imprint","IMPRINT",EDGE,{"disambiguationData":[TD([[subQ55,-1.0]])],"derivedFrom":subQ12}),makeQuery(id+"F5.imprint","IMPRINT",EDGE,{"disambiguationData":[TD([[subQ57,-1.0]])],"derivedFrom":subQ2}),makeQuery(id+"F5.imprint","IMPRINT",EDGE,{"disambiguationData":[TD([[subQ51,-1.0]])],"derivedFrom":subQ50}),makeQuery(id+"F5.imprint","IMPRINT",EDGE,{"disambiguationData":[TD([[subQ55,-1.0]])],"derivedFrom":subQ54})])],"isStart":true}),makeQuery(id+"F6.opExtrude","CAP_FACE",FACE,{"disambiguationData":[OSD([subQ12,subQ2,subQ46,subQ50]),TDD([makeQuery(id+"F5.imprint","IMPRINT",EDGE,{"disambiguationData":[TD([[subQ51,-1.0]])],"derivedFrom":subQ12}),makeQuery(id+"F5.imprint","IMPRINT",EDGE,{"disambiguationData":[TD([[subQ52,-1.0]])],"derivedFrom":subQ2}),makeQuery(id+"F5.imprint","IMPRINT",EDGE,{"disambiguationData":[TD([[subQ47,1.0]])],"derivedFrom":subQ46}),makeQuery(id+"F5.imprint","IMPRINT",EDGE,{"disambiguationData":[TD([[subQ51,1.0]])],"derivedFrom":subQ50})])],"isStart":true}),makeQuery(id+"F6.opExtrude","CAP_FACE",FACE,{"disambiguationData":[OSD([subQ12,subQ2,subQ42,subQ46]),TDD([makeQuery(id+"F5.imprint","IMPRINT",EDGE,{"disambiguationData":[TD([[subQ47,-1.0]])],"derivedFrom":subQ12}),makeQuery(id+"F5.imprint","IMPRINT",EDGE,{"disambiguationData":[TD([[subQ49,-1.0]])],"derivedFrom":subQ2}),makeQuery(id+"F5.imprint","IMPRINT",EDGE,{"disambiguationData":[TD([[subQ43,-1.0]])],"derivedFrom":subQ42}),makeQuery(id+"F5.imprint","IMPRINT",EDGE,{"disambiguationData":[TD([[subQ47,-1.0]])],"derivedFrom":subQ46})])],"isStart":true}),makeQuery(id+"F6.opExtrude","CAP_FACE",FACE,{"disambiguationData":[OSD([subQ12,subQ2,subQ38,subQ42]),TDD([makeQuery(id+"F5.imprint","IMPRINT",EDGE,{"disambiguationData":[TD([[subQ43,-1.0]])],"derivedFrom":subQ12}),makeQuery(id+"F5.imprint","IMPRINT",EDGE,{"disambiguationData":[TD([[subQ44,-1.0]])],"derivedFrom":subQ2}),makeQuery(id+"F5.imprint","IMPRINT",EDGE,{"disambiguationData":[TD([[subQ39,1.0]])],"derivedFrom":subQ38}),makeQuery(id+"F5.imprint","IMPRINT",EDGE,{"disambiguationData":[TD([[subQ43,1.0]])],"derivedFrom":subQ42})])],"isStart":true}),makeQuery(id+"F6.opExtrude","CAP_FACE",FACE,{"disambiguationData":[OSD([subQ12,subQ2,subQ34,subQ38]),TDD([makeQuery(id+"F5.imprint","IMPRINT",EDGE,{"disambiguationData":[TD([[subQ39,-1.0]])],"derivedFrom":subQ12}),makeQuery(id+"F5.imprint","IMPRINT",EDGE,{"disambiguationData":[TD([[subQ41,-1.0]])],"derivedFrom":subQ2}),makeQuery(id+"F5.imprint","IMPRINT",EDGE,{"disambiguationData":[TD([[subQ35,-1.0]])],"derivedFrom":subQ34}),makeQuery(id+"F5.imprint","IMPRINT",EDGE,{"disambiguationData":[TD([[subQ39,-1.0]])],"derivedFrom":subQ38})])],"isStart":true}),makeQuery(id+"F6.opExtrude","CAP_FACE",FACE,{"disambiguationData":[OSD([subQ12,subQ2,subQ30,subQ34]),TDD([makeQuery(id+"F5.imprint","IMPRINT",EDGE,{"disambiguationData":[TD([[subQ35,-1.0]])],"derivedFrom":subQ12}),makeQuery(id+"F5.imprint","IMPRINT",EDGE,{"disambiguationData":[TD([[subQ36,-1.0]])],"derivedFrom":subQ2}),makeQuery(id+"F5.imprint","IMPRINT",EDGE,{"disambiguationData":[TD([[subQ31,1.0]])],"derivedFrom":subQ30}),makeQuery(id+"F5.imprint","IMPRINT",EDGE,{"disambiguationData":[TD([[subQ35,1.0]])],"derivedFrom":subQ34})])],"isStart":true}),makeQuery(id+"F6.opExtrude","CAP_FACE",FACE,{"disambiguationData":[OSD([subQ12,subQ2,subQ26,subQ30]),TDD([makeQuery(id+"F5.imprint","IMPRINT",EDGE,{"disambiguationData":[TD([[subQ31,-1.0]])],"derivedFrom":subQ12}),makeQuery(id+"F5.imprint","IMPRINT",EDGE,{"disambiguationData":[TD([[subQ33,-1.0]])],"derivedFrom":subQ2}),makeQuery(id+"F5.imprint","IMPRINT",EDGE,{"disambiguationData":[TD([[subQ27,-1.0]])],"derivedFrom":subQ26}),makeQuery(id+"F5.imprint","IMPRINT",EDGE,{"disambiguationData":[TD([[subQ31,-1.0]])],"derivedFrom":subQ30})])],"isStart":true}),makeQuery(id+"F6.opExtrude","CAP_FACE",FACE,{"disambiguationData":[OSD([subQ12,subQ2,subQ22,subQ26]),TDD([makeQuery(id+"F5.imprint","IMPRINT",EDGE,{"disambiguationData":[TD([[subQ27,-1.0]])],"derivedFrom":subQ12}),makeQuery(id+"F5.imprint","IMPRINT",EDGE,{"disambiguationData":[TD([[subQ28,-1.0]])],"derivedFrom":subQ2}),makeQuery(id+"F5.imprint","IMPRINT",EDGE,{"disambiguationData":[TD([[subQ23,1.0]])],"derivedFrom":subQ22}),makeQuery(id+"F5.imprint","IMPRINT",EDGE,{"disambiguationData":[TD([[subQ27,1.0]])],"derivedFrom":subQ26})])],"isStart":true}),makeQuery(id+"F6.opExtrude","CAP_FACE",FACE,{"disambiguationData":[OSD([subQ12,subQ2,subQ18,subQ22]),TDD([makeQuery(id+"F5.imprint","IMPRINT",EDGE,{"disambiguationData":[TD([[subQ23,-1.0]])],"derivedFrom":subQ12}),makeQuery(id+"F5.imprint","IMPRINT",EDGE,{"disambiguationData":[TD([[subQ25,-1.0]])],"derivedFrom":subQ2}),makeQuery(id+"F5.imprint","IMPRINT",EDGE,{"disambiguationData":[TD([[subQ19,-1.0]])],"derivedFrom":subQ18}),makeQuery(id+"F5.imprint","IMPRINT",EDGE,{"disambiguationData":[TD([[subQ23,-1.0]])],"derivedFrom":subQ22})])],"isStart":true}),makeQuery(id+"F6.opExtrude","CAP_FACE",FACE,{"disambiguationData":[OSD([subQ12,subQ2,subQ13,subQ18]),TDD([makeQuery(id+"F5.imprint","IMPRINT",EDGE,{"disambiguationData":[TD([[subQ19,-1.0]])],"derivedFrom":subQ12}),makeQuery(id+"F5.imprint","IMPRINT",EDGE,{"disambiguationData":[TD([[subQ20,-1.0]])],"derivedFrom":subQ2}),makeQuery(id+"F5.imprint","IMPRINT",EDGE,{"disambiguationData":[TD([[subQ14,1.0]])],"derivedFrom":subQ13}),makeQuery(id+"F5.imprint","IMPRINT",EDGE,{"disambiguationData":[TD([[subQ19,1.0]])],"derivedFrom":subQ18})])],"isStart":true}),makeQuery(id+"F6.opExtrude","CAP_FACE",FACE,{"disambiguationData":[OSD([subQ12,subQ2,subQ0,subQ13]),TDD([makeQuery(id+"F5.imprint","IMPRINT",EDGE,{"disambiguationData":[TD([[subQ14,-1.0]])],"derivedFrom":subQ12}),makeQuery(id+"F5.imprint","IMPRINT",EDGE,{"disambiguationData":[TD([[subQ17,-1.0]])],"derivedFrom":subQ2}),makeQuery(id+"F5.imprint","IMPRINT",EDGE,{"disambiguationData":[TD([[subQ16,-1.0]])],"derivedFrom":subQ0}),makeQuery(id+"F5.imprint","IMPRINT",EDGE,{"disambiguationData":[TD([[subQ14,-1.0]])],"derivedFrom":subQ13})])],"isStart":true}),makeQuery(id+"F6.boolean.opBoolean","MERGE",FACE,{"derivedFrom":[makeQuery(id+"F3.boolean.opBoolean","MERGE",FACE,{"derivedFrom":[makeQuery(id+"F1.opExtrude","SWEPT_FACE",FACE,{"disambiguationData":[OSD([subQ11])]}),makeQuery(id+"F3.opExtrude","CAP_FACE",FACE,{"disambiguationData":[OSD([subQ10,subQ9,subQ8,subQ7,subQ6,subQ5,subQ4,subQ3])],"isStart":true})]}),makeQuery(id+"F6.opExtrude","CAP_FACE",FACE,{"disambiguationData":[OSD([subQ11,subQ10,subQ9,subQ8,subQ7,subQ6,subQ5,subQ4,subQ3,subQ12,subQ1,subQ0])],"isStart":true}),makeQuery(id+"F6.opExtrude","CAP_FACE",FACE,{"disambiguationData":[OSD([subQ11,subQ10,subQ9,subQ8,subQ7,subQ6,subQ5,subQ4,subQ3,subQ12,subQ2,subQ1,subQ0])],"isStart":true}),makeQuery(id+"F6.opExtrude","CAP_FACE",FACE,{"disambiguationData":[OSD([subQ11,subQ10,subQ9,subQ8,subQ7,subQ6,subQ5,subQ4,subQ3,subQ2,subQ1,subQ0])],"isStart":true})]}),makeQuery(id+"F8.opExtrude","CAP_FACE",FACE,{"disambiguationData":[OSD([sQuery(id+"F7.wireOp",EDGE,"E19"),sQuery(id+"F7.wireOp",EDGE,"E20"),sQuery(id+"F7.wireOp",EDGE,"E21"),sQuery(id+"F7.wireOp",EDGE,"E22"),sQuery(id+"F7.wireOp",EDGE,"E23"),sQuery(id+"F7.wireOp",EDGE,"E24"),sQuery(id+"F7.wireOp",EDGE,"E25"),sQuery(id+"F7.wireOp",EDGE,"E26")])],"isStart":true})]}),makeQuery(id+"FZaE8QNVp6XG5ye_1.opExtrude","CAP_FACE",FACE,{"disambiguationData":[OSD([sQuery(id+"FQdyxd8xbATGqtn_1.wireOp",EDGE,"xDT7U143-1ZfQ-tOo5-LNQv-eCxHP1mS58vr"),sQuery(id+"FQdyxd8xbATGqtn_1.wireOp",EDGE,"FlZFNKmO-1mFb-dZK1-pEXj-0cqHaFgLSyFe")])],"isStart":true})]});}
            var Q3;
            Q3=makeQuery(id+"F3.boolean.opBoolean","MERGE",FACE,{"derivedFrom":[makeQuery(id+"F1.opExtrude","SWEPT_FACE",FACE,{"disambiguationData":[OSD([sQuery(id+"F0.wireOp",EDGE,"E0.bottom")])]}),makeQuery(id+"F3.opExtrude","CAP_FACE",FACE,{"disambiguationData":[OSD([sQuery(id+"F2.wireOp",EDGE,"E1.bottom"),sQuery(id+"F2.wireOp",EDGE,"E1.top"),sQuery(id+"F2.wireOp",EDGE,"E1.left"),sQuery(id+"F2.wireOp",EDGE,"E1.right"),sQuery(id+"F2.wireOp",EDGE,"E2.bottom"),sQuery(id+"F2.wireOp",EDGE,"E2.top"),sQuery(id+"F2.wireOp",EDGE,"E2.left"),sQuery(id+"F2.wireOp",EDGE,"E2.right")])],"isStart":false})]});
            fillet(context, id + "F9", {"entities" : qUnion([Q0, Q1, Q2, Q3]), "radius" : 1 * mm, "tangentPropagation" : true, "allowEdgeOverflow" : false});
        }
    });
